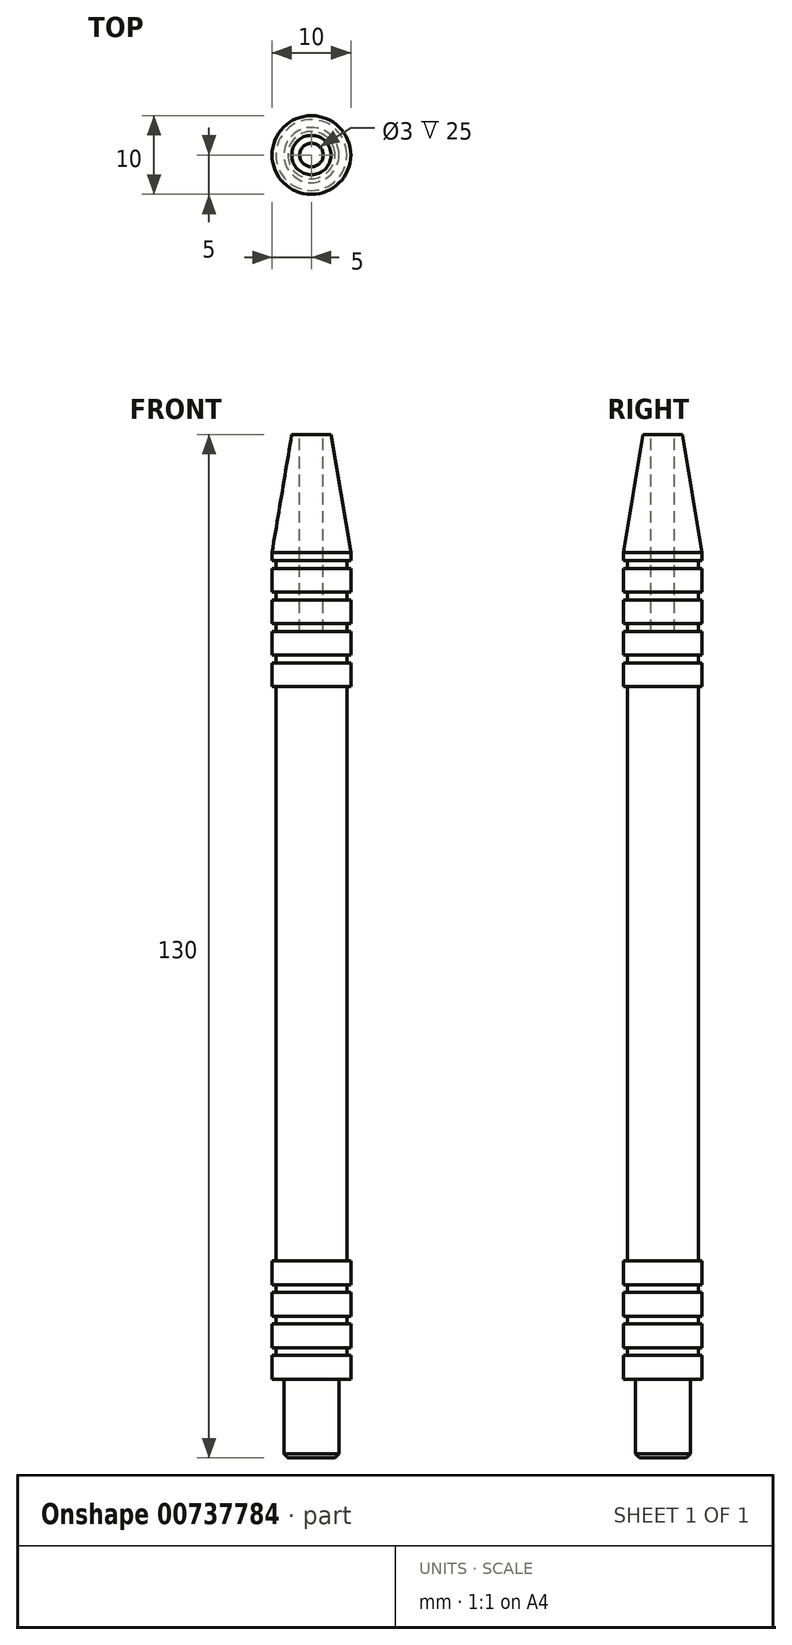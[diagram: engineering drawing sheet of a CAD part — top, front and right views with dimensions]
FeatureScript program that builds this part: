
annotation { "Feature Type Name" : "Feature", "Feature Type Description" : "" }
export const myFeature = defineFeature(function(context is Context, id is Id, definition is map)
    precondition{}
    {
        {
            var Q0;
            Q0=qCreatedBy(makeId("Front.planeOp"),FACE);
            var sketch = newSketch(context, id + "F0", { "sketchPlane" : qUnion([Q0])});
            skLineSegment(sketch, "E0", {"start": v(0, 0) * mm, "end": v(0, 130) * mm});
            skLineSegment(sketch, "E1", {"start": v(0, 130) * mm, "end": v(2.5, 130) * mm});
            skLineSegment(sketch, "E2", {"start": v(2.5, 130) * mm, "end": v(5, 115) * mm});
            skLineSegment(sketch, "E3", {"start": v(0, 0) * mm, "end": v(3.5, 0) * mm});
            skLineSegment(sketch, "E4", {"start": v(3.5, 0) * mm, "end": v(3.5, 10) * mm});
            skLineSegment(sketch, "E5", {"start": v(3.5, 10) * mm, "end": v(5, 10) * mm});
            skLineSegment(sketch, "E6", {"start": v(5, 10) * mm, "end": v(5, 13) * mm});
            skLineSegment(sketch, "E7", {"start": v(5, 13) * mm, "end": v(4.5, 13) * mm});
            skLineSegment(sketch, "E8", {"start": v(4.5, 13) * mm, "end": v(4.5, 14) * mm});
            skLineSegment(sketch, "E9", {"start": v(4.5, 14) * mm, "end": v(5, 14) * mm});
            skLineSegment(sketch, "E10", {"start": v(5, 14) * mm, "end": v(5, 17) * mm});
            skLineSegment(sketch, "E11", {"start": v(5, 17) * mm, "end": v(4.5, 17) * mm});
            skLineSegment(sketch, "E12", {"start": v(4.5, 17) * mm, "end": v(4.5, 18) * mm});
            skLineSegment(sketch, "E13", {"start": v(4.5, 18) * mm, "end": v(5, 18) * mm});
            skLineSegment(sketch, "E14", {"start": v(5, 18) * mm, "end": v(5, 21) * mm});
            skLineSegment(sketch, "E15", {"start": v(5, 21) * mm, "end": v(4.5, 21) * mm});
            skLineSegment(sketch, "E16", {"start": v(4.5, 21) * mm, "end": v(4.5, 22) * mm});
            skLineSegment(sketch, "E17", {"start": v(4.5, 22) * mm, "end": v(5, 22) * mm});
            skLineSegment(sketch, "E18", {"start": v(5, 22) * mm, "end": v(5, 25) * mm});
            skLineSegment(sketch, "E19", {"start": v(5, 25) * mm, "end": v(4.5, 25) * mm});
            skLineSegment(sketch, "E20", {"start": v(5, 115) * mm, "end": v(5, 114) * mm});
            skLineSegment(sketch, "E21", {"start": v(5, 114) * mm, "end": v(4.5, 114) * mm});
            skLineSegment(sketch, "E22", {"start": v(4.5, 114) * mm, "end": v(4.5, 113) * mm});
            skLineSegment(sketch, "E23", {"start": v(4.5, 113) * mm, "end": v(5, 113) * mm});
            skLineSegment(sketch, "E24", {"start": v(5, 113) * mm, "end": v(5, 110) * mm});
            skLineSegment(sketch, "E25", {"start": v(5, 110) * mm, "end": v(4.5, 110) * mm});
            skLineSegment(sketch, "E26", {"start": v(4.5, 110) * mm, "end": v(4.5, 109) * mm});
            skLineSegment(sketch, "E27", {"start": v(4.5, 109) * mm, "end": v(5, 109) * mm});
            skLineSegment(sketch, "E28", {"start": v(5, 109) * mm, "end": v(5, 106) * mm});
            skLineSegment(sketch, "E29", {"start": v(5, 106) * mm, "end": v(4.5, 106) * mm});
            skLineSegment(sketch, "E30", {"start": v(4.5, 106) * mm, "end": v(4.5, 105) * mm});
            skLineSegment(sketch, "E31", {"start": v(4.5, 105) * mm, "end": v(5, 105) * mm});
            skLineSegment(sketch, "E32", {"start": v(5, 105) * mm, "end": v(5, 102) * mm});
            skLineSegment(sketch, "E33", {"start": v(5, 102) * mm, "end": v(4.5, 102) * mm});
            skLineSegment(sketch, "E34", {"start": v(4.5, 102) * mm, "end": v(4.5, 101) * mm});
            skLineSegment(sketch, "E35", {"start": v(4.5, 101) * mm, "end": v(5, 101) * mm});
            skLineSegment(sketch, "E36", {"start": v(5, 101) * mm, "end": v(5, 98) * mm});
            skLineSegment(sketch, "E37", {"start": v(5, 98) * mm, "end": v(4.5, 98) * mm});
            skLineSegment(sketch, "E38", {"start": v(4.5, 25) * mm, "end": v(4.5, 98) * mm});
            skSolve(sketch);
        }
        {
            var Q0;
            Q0=makeQuery(id+"F0.imprint","IMPRINT",FACE,{"disambiguationData":[TD([[makeQuery(id+"F0.imprint","IMPRINT",EDGE,{"derivedFrom":sQuery(id+"F0.wireOp",EDGE,"E0")}),-1.0]])]});
            var Q1;
            Q1=sQuery(id+"F0.wireOp",EDGE,"E0");
            revolve(context, id + "F1", {"surfaceOperationType" : NewSurfaceOperationType.NEW, "entities" : qUnion([Q0]), "axis" : qUnion([Q1]), "revolveType" : RevolveType.FULL});
        }
        {
            var Q0;
            Q0=makeQuery(id+"F1.opRevolve","SWEPT_FACE",FACE,{"disambiguationData":[OSD([sQuery(id+"F0.wireOp",EDGE,"E1")])]});
            var sketch = newSketch(context, id + "F2", { "sketchPlane" : qUnion([Q0])});
            skCircle(sketch, "E39", {"center": v(0, 0) * mm, "radius": 1.5 * mm});
            skSolve(sketch);
        }
        {
            var Q0;
            Q0=makeQuery(id+"F2.imprint","IMPRINT",FACE,{"disambiguationData":[TD([[makeQuery(id+"F2.imprint","IMPRINT",EDGE,{"derivedFrom":sQuery(id+"F2.wireOp",EDGE,"E39")}),1.0]])]});
            extrude(context, id + "F3", {"entities" : qUnion([Q0]), "operationType" : NewBodyOperationType.REMOVE, "oppositeDirection" : true, "depth" : 25 * mm, "offsetDistance" : 25 * mm});
        }
        {
            var Q0;
            Q0=makeQuery(id+"F1.opRevolve","SWEPT_EDGE",EDGE,{"disambiguationData":[OSD([sQuery(id+"F0.wireOp",EDGE,"E3"),sQuery(id+"F0.wireOp",EDGE,"E4")])]});
            chamfer(context, id + "F4", {"entities" : qUnion([Q0]), "width" : 0.5 * mm, "tangentPropagation" : true});
        }
    });
